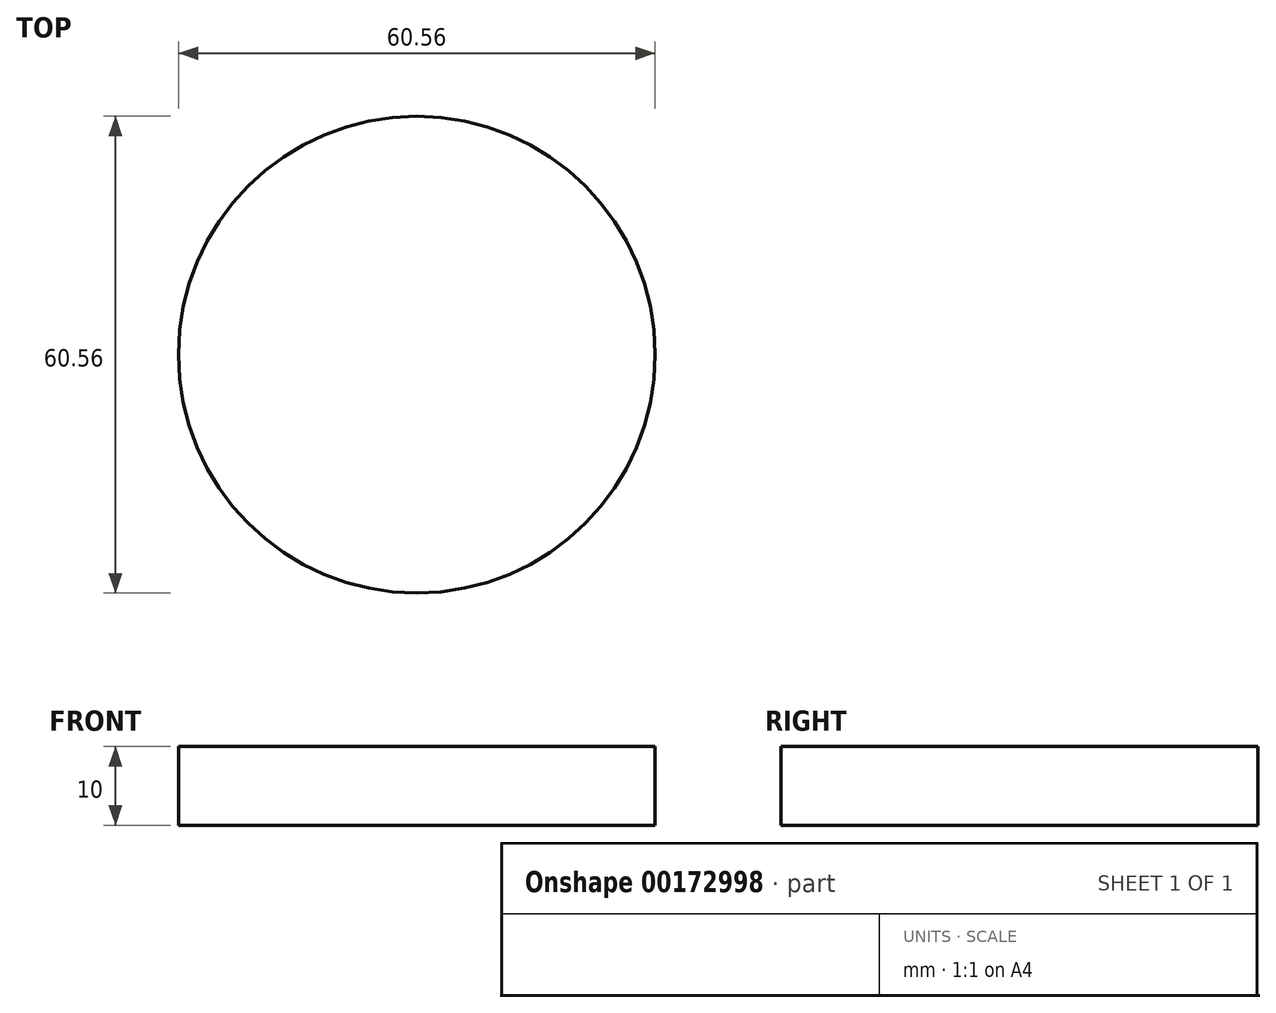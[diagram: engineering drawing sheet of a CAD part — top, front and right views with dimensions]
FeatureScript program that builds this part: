
annotation { "Feature Type Name" : "Feature", "Feature Type Description" : "" }
export const myFeature = defineFeature(function(context is Context, id is Id, definition is map)
    precondition{}
    {
        {
            var Q0;
            Q0=qCreatedBy(makeId("Top.planeOp"),FACE);
            var sketch = newSketch(context, id + "F0", { "sketchPlane" : qUnion([Q0])});
            skCircle(sketch, "E0", {"center": v(0, 0) * mm, "radius": 30.28 * mm});
            skSolve(sketch);
        }
        {
            var Q0;
            Q0 = qSketchRegion(id + "F0", true);
            extrude(context, id + "F1", {"entities" : qUnion([Q0]), "depth" : 10 * mm});
        }
    });
